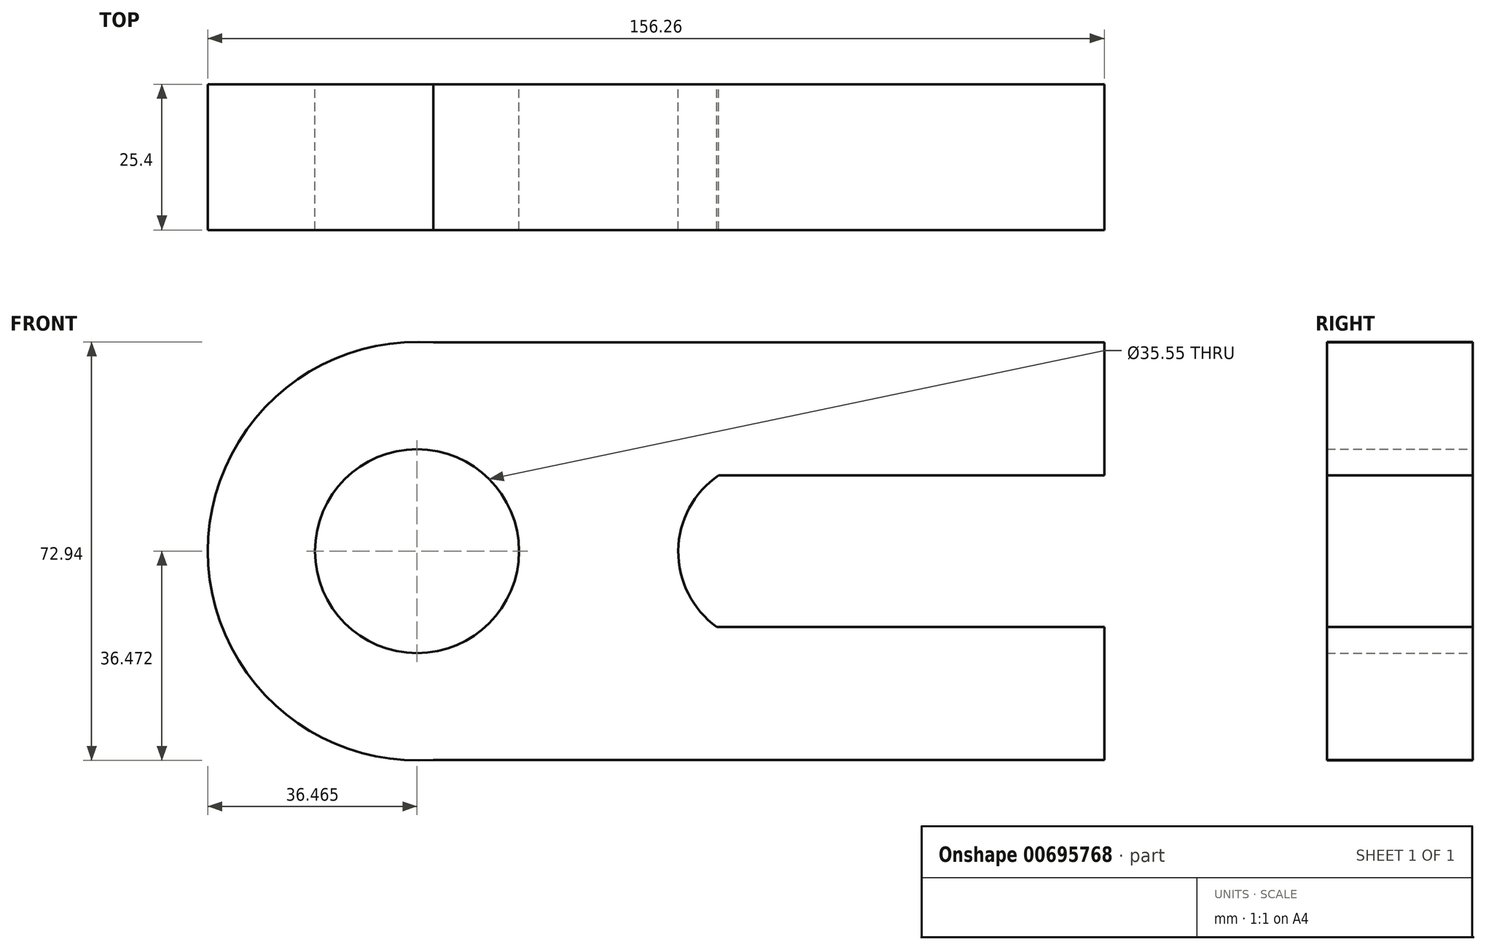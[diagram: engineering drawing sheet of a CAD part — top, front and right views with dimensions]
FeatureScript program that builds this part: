
annotation { "Feature Type Name" : "Feature", "Feature Type Description" : "" }
export const myFeature = defineFeature(function(context is Context, id is Id, definition is map)
    precondition{}
    {
        {
            var Q0;
            Q0=qCreatedBy(makeId("Front.planeOp"),FACE);
            var sketch = newSketch(context, id + "F0", { "sketchPlane" : qUnion([Q0])});
            skCircle(sketch, "E0", {"center": v(-69.44, 18.21) * mm, "radius": 36.47 * mm});
            skCircle(sketch, "E1", {"center": v(-69.44, 18.21) * mm, "radius": 17.78 * mm});
            skLineSegment(sketch, "E2", {"start": v(-66.59, 54.57) * mm, "end": v(50.35, 54.57) * mm});
            skLineSegment(sketch, "E3", {"start": v(50.35, 54.57) * mm, "end": v(50.35, 31.42) * mm});
            skLineSegment(sketch, "E4", {"start": v(50.35, 31.42) * mm, "end": v(-16.88, 31.42) * mm});
            skLineSegment(sketch, "E5", {"start": v(-17.18, 5) * mm, "end": v(50.35, 5) * mm});
            skLineSegment(sketch, "E6", {"start": v(-66.59, -18.14) * mm, "end": v(50.35, -18.14) * mm});
            skLineSegment(sketch, "E7", {"start": v(50.35, 5) * mm, "end": v(50.35, -18.14) * mm});
            skArc(sketch, "E8", {"start": v(50.35, 50.8) * mm, "mid": v(45.72, 53.46) * mm, "end": v(40.5, 54.57) * mm});
            skArc(sketch, "E9", {"start": v(-16.88, 31.42) * mm, "mid": v(-23.92, 18.29) * mm, "end": v(-17.18, 5) * mm});
            skSolve(sketch);
        }
        {
            var Q0;
            Q0 = qSketchRegion(id + "F0", true);
            extrude(context, id + "F1", {"entities" : qUnion([Q0]), "depth" : 25.4 * mm, "offsetDistance" : 25.4 * mm});
        }
    });
